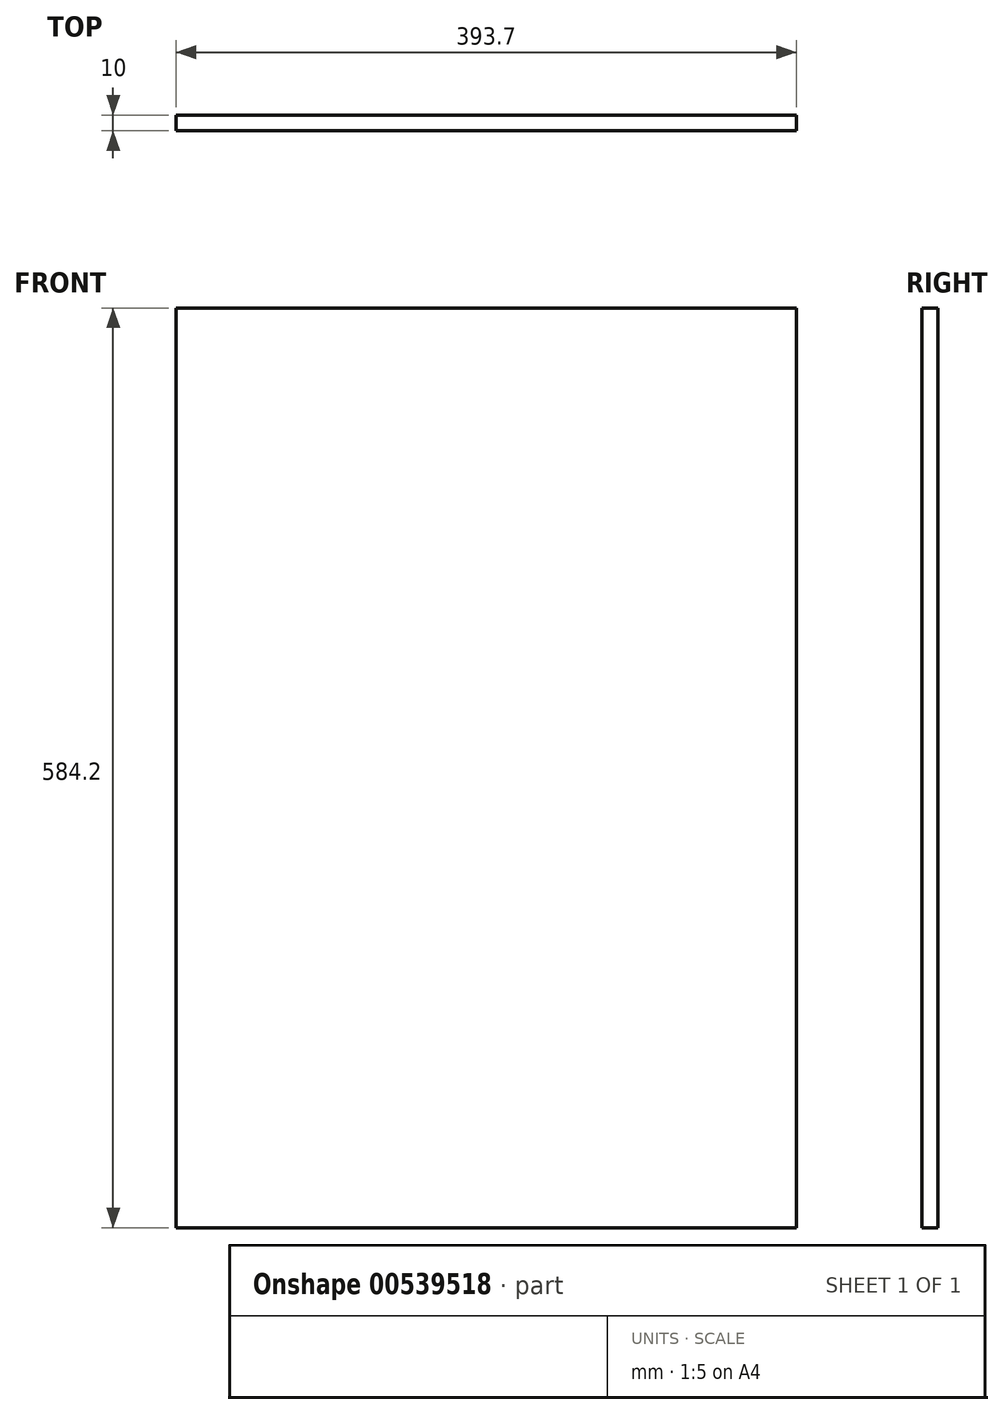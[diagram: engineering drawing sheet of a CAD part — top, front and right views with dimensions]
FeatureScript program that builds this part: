
annotation { "Feature Type Name" : "Feature", "Feature Type Description" : "" }
export const myFeature = defineFeature(function(context is Context, id is Id, definition is map)
    precondition{}
    {
        {
            var Q0;
            Q0=qCreatedBy(makeId("Front.planeOp"),FACE);
            var sketch = newSketch(context, id + "F0", { "sketchPlane" : qUnion([Q0])});
            skLineSegment(sketch, "E0.bottom", {"start": v(196.85, -292.1) * mm, "end": v(-196.85, -292.1) * mm});
            skLineSegment(sketch, "E0.top", {"start": v(196.85, 292.1) * mm, "end": v(-196.85, 292.1) * mm});
            skLineSegment(sketch, "E0.left", {"start": v(196.85, -292.1) * mm, "end": v(196.85, 292.1) * mm});
            skLineSegment(sketch, "E0.right", {"start": v(-196.85, -292.1) * mm, "end": v(-196.85, 292.1) * mm});
            skPoint(sketch, "E0.middle", {"position": v(0, 0) * mm});
            skSolve(sketch);
        }
        {
            var Q0;
            Q0=makeQuery(id+"F0.imprint","IMPRINT",FACE,{"disambiguationData":[TD([[makeQuery(id+"F0.imprint","IMPRINT",EDGE,{"derivedFrom":sQuery(id+"F0.wireOp",EDGE,"E0.bottom")}),-1.0]])]});
            extrude(context, id + "F1", {"entities" : qUnion([Q0]), "depth" : 10 * mm});
        }
    });
